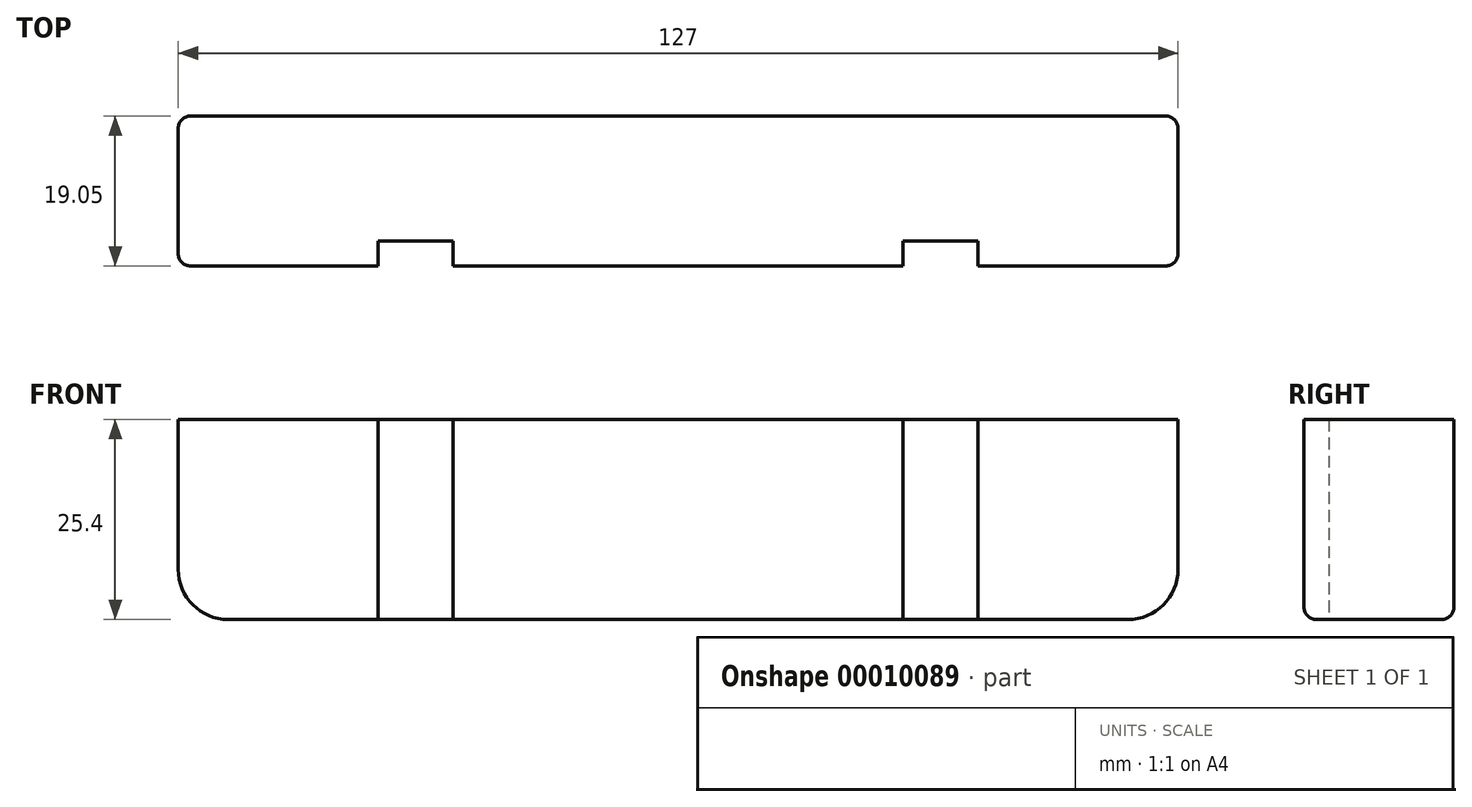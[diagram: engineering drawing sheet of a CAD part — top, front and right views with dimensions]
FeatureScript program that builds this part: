
annotation { "Feature Type Name" : "Feature", "Feature Type Description" : "" }
export const myFeature = defineFeature(function(context is Context, id is Id, definition is map)
    precondition{}
    {
        {
            var Q0;
            Q0=qCreatedBy(makeId("Front.planeOp"),FACE);
            var sketch = newSketch(context, id + "F0", { "sketchPlane" : qUnion([Q0])});
            skLineSegment(sketch, "E0.rect.bottom", {"start": v(63.5, 12.7) * mm, "end": v(-63.5, 12.7) * mm});
            skLineSegment(sketch, "E0.rect.top", {"start": v(63.5, -12.7) * mm, "end": v(-63.5, -12.7) * mm});
            skLineSegment(sketch, "E0.rect.left", {"start": v(63.5, 12.7) * mm, "end": v(63.5, -12.7) * mm});
            skLineSegment(sketch, "E0.rect.right", {"start": v(-63.5, 12.7) * mm, "end": v(-63.5, -12.7) * mm});
            skPoint(sketch, "E0.rect.middle", {"position": v(0, 0) * mm});
            skSolve(sketch);
        }
        {
            var Q0;
            Q0=makeQuery(id+"F0.imprint","IMPRINT",FACE,{"disambiguationData":[TD([[makeQuery(id+"F0.imprint","IMPRINT",EDGE,{"derivedFrom":sQuery(id+"F0.wireOp",EDGE,"E0.rect.bottom")}),1.0]])]});
            extrude(context, id + "F1", {"entities" : qUnion([Q0]), "oppositeDirection" : true, "depth" : 19.05 * mm});
        }
        {
            var Q0;
            Q0=makeQuery(id+"F1.opExtrude","SWEPT_EDGE",EDGE,{"disambiguationData":[OSD([sQuery(id+"F0.wireOp",EDGE,"E0.rect.top"),sQuery(id+"F0.wireOp",EDGE,"E0.rect.left")])]});
            var Q1;
            Q1=makeQuery(id+"F1.opExtrude","SWEPT_EDGE",EDGE,{"disambiguationData":[OSD([sQuery(id+"F0.wireOp",EDGE,"E0.rect.top"),sQuery(id+"F0.wireOp",EDGE,"E0.rect.right")])]});
            fillet(context, id + "F2", {"entities" : qUnion([Q0, Q1]), "radius" : 6.35 * mm, "tangentPropagation" : true, "allowEdgeOverflow" : false});
        }
        {
            var Q0;
            Q0=makeQuery(id+"F1.opExtrude","CAP_EDGE",EDGE,{"disambiguationData":[OSD([sQuery(id+"F0.wireOp",EDGE,"E0.rect.right")])],"isStart":true});
            var Q1;
            {var subQ0=sQuery(id+"F0.wireOp",EDGE,"E0.rect.top");var subQ1=sQuery(id+"F0.wireOp",EDGE,"E0.rect.right");Q1=makeQuery(id+"F2.opFillet","BLEND_EDGE",EDGE,{"blendedFrom":[makeQuery(id+"F1.opExtrude","SWEPT_EDGE",EDGE,{"disambiguationData":[OSD([subQ0,subQ1])]}),makeQuery(id+"F1.opExtrude","CAP_FACE",FACE,{"disambiguationData":[OSD([sQuery(id+"F0.wireOp",EDGE,"E0.rect.bottom"),subQ0,sQuery(id+"F0.wireOp",EDGE,"E0.rect.left"),subQ1])],"isStart":true})],"blendedInto":[makeQuery(id+"F1.opExtrude","CAP_FACE",FACE,{"disambiguationData":[OSD([sQuery(id+"F0.wireOp",EDGE,"E0.rect.bottom"),subQ0,sQuery(id+"F0.wireOp",EDGE,"E0.rect.left"),subQ1])],"isStart":true})]});}
            var Q2;
            Q2=makeQuery(id+"F1.opExtrude","CAP_EDGE",EDGE,{"disambiguationData":[OSD([sQuery(id+"F0.wireOp",EDGE,"E0.rect.top")])],"isStart":true});
            var Q3;
            {var subQ0=sQuery(id+"F0.wireOp",EDGE,"E0.rect.top");var subQ1=sQuery(id+"F0.wireOp",EDGE,"E0.rect.left");Q3=makeQuery(id+"F2.opFillet","BLEND_EDGE",EDGE,{"blendedFrom":[makeQuery(id+"F1.opExtrude","SWEPT_EDGE",EDGE,{"disambiguationData":[OSD([subQ0,subQ1])]}),makeQuery(id+"F1.opExtrude","CAP_FACE",FACE,{"disambiguationData":[OSD([sQuery(id+"F0.wireOp",EDGE,"E0.rect.bottom"),subQ0,subQ1,sQuery(id+"F0.wireOp",EDGE,"E0.rect.right")])],"isStart":true})],"blendedInto":[makeQuery(id+"F1.opExtrude","CAP_FACE",FACE,{"disambiguationData":[OSD([sQuery(id+"F0.wireOp",EDGE,"E0.rect.bottom"),subQ0,subQ1,sQuery(id+"F0.wireOp",EDGE,"E0.rect.right")])],"isStart":true})]});}
            var Q4;
            Q4=makeQuery(id+"F1.opExtrude","CAP_EDGE",EDGE,{"disambiguationData":[OSD([sQuery(id+"F0.wireOp",EDGE,"E0.rect.left")])],"isStart":true});
            var Q5;
            Q5=makeQuery(id+"F1.opExtrude","CAP_EDGE",EDGE,{"disambiguationData":[OSD([sQuery(id+"F0.wireOp",EDGE,"E0.rect.left")])],"isStart":false});
            var Q6;
            {var subQ0=sQuery(id+"F0.wireOp",EDGE,"E0.rect.top");var subQ1=sQuery(id+"F0.wireOp",EDGE,"E0.rect.left");Q6=makeQuery(id+"F2.opFillet","BLEND_EDGE",EDGE,{"blendedFrom":[makeQuery(id+"F1.opExtrude","SWEPT_EDGE",EDGE,{"disambiguationData":[OSD([subQ0,subQ1])]}),makeQuery(id+"F1.opExtrude","CAP_FACE",FACE,{"disambiguationData":[OSD([sQuery(id+"F0.wireOp",EDGE,"E0.rect.bottom"),subQ0,subQ1,sQuery(id+"F0.wireOp",EDGE,"E0.rect.right")])],"isStart":false})],"blendedInto":[makeQuery(id+"F1.opExtrude","CAP_FACE",FACE,{"disambiguationData":[OSD([sQuery(id+"F0.wireOp",EDGE,"E0.rect.bottom"),subQ0,subQ1,sQuery(id+"F0.wireOp",EDGE,"E0.rect.right")])],"isStart":false})]});}
            var Q7;
            Q7=makeQuery(id+"F1.opExtrude","CAP_EDGE",EDGE,{"disambiguationData":[OSD([sQuery(id+"F0.wireOp",EDGE,"E0.rect.top")])],"isStart":false});
            var Q8;
            {var subQ0=sQuery(id+"F0.wireOp",EDGE,"E0.rect.top");var subQ1=sQuery(id+"F0.wireOp",EDGE,"E0.rect.right");Q8=makeQuery(id+"F2.opFillet","BLEND_EDGE",EDGE,{"blendedFrom":[makeQuery(id+"F1.opExtrude","SWEPT_EDGE",EDGE,{"disambiguationData":[OSD([subQ0,subQ1])]}),makeQuery(id+"F1.opExtrude","CAP_FACE",FACE,{"disambiguationData":[OSD([sQuery(id+"F0.wireOp",EDGE,"E0.rect.bottom"),subQ0,sQuery(id+"F0.wireOp",EDGE,"E0.rect.left"),subQ1])],"isStart":false})],"blendedInto":[makeQuery(id+"F1.opExtrude","CAP_FACE",FACE,{"disambiguationData":[OSD([sQuery(id+"F0.wireOp",EDGE,"E0.rect.bottom"),subQ0,sQuery(id+"F0.wireOp",EDGE,"E0.rect.left"),subQ1])],"isStart":false})]});}
            var Q9;
            Q9=makeQuery(id+"F1.opExtrude","CAP_EDGE",EDGE,{"disambiguationData":[OSD([sQuery(id+"F0.wireOp",EDGE,"E0.rect.right")])],"isStart":false});
            fillet(context, id + "F3", {"entities" : qUnion([Q0, Q1, Q2, Q3, Q4, Q5, Q6, Q7, Q8, Q9]), "radius" : 1.59 * mm, "allowEdgeOverflow" : false});
        }
        {
            var Q0;
            Q0=makeQuery(id+"F1.opExtrude","CAP_FACE",FACE,{"disambiguationData":[OSD([sQuery(id+"F0.wireOp",EDGE,"E0.rect.bottom"),sQuery(id+"F0.wireOp",EDGE,"E0.rect.top"),sQuery(id+"F0.wireOp",EDGE,"E0.rect.left"),sQuery(id+"F0.wireOp",EDGE,"E0.rect.right")])],"isStart":true});
            var sketch = newSketch(context, id + "F4", { "sketchPlane" : qUnion([Q0])});
            skLineSegment(sketch, "E1.0", {"start": v(57.15, -12.7) * mm, "end": v(-57.15, -12.7) * mm});
            skLineSegment(sketch, "E2.bottom", {"start": v(-28.57, 12.7) * mm, "end": v(-38.1, 12.7) * mm});
            skLineSegment(sketch, "E2.top", {"start": v(-28.57, -12.7) * mm, "end": v(-38.1, -12.7) * mm});
            skLineSegment(sketch, "E2.left", {"start": v(-28.57, 12.7) * mm, "end": v(-28.57, -12.7) * mm});
            skLineSegment(sketch, "E2.right", {"start": v(-38.1, 12.7) * mm, "end": v(-38.1, -12.7) * mm});
            skLineSegment(sketch, "E3", {"start": v(0, 12.7) * mm, "end": v(0, -12.7) * mm, "construction": true});
            skLineSegment(sketch, "E4.MirrorCS", {"start": v(28.57, 12.7) * mm, "end": v(38.1, 12.7) * mm});
            skLineSegment(sketch, "E5.MirrorCS", {"start": v(28.58, -12.7) * mm, "end": v(38.1, -12.7) * mm});
            skLineSegment(sketch, "E6.MirrorCS", {"start": v(38.1, 12.7) * mm, "end": v(38.1, -12.7) * mm});
            skLineSegment(sketch, "E7.MirrorCS", {"start": v(28.57, 12.7) * mm, "end": v(28.58, -12.7) * mm});
            skSolve(sketch);
        }
        {
            var Q0;
            Q0 = qSketchRegion(id + "F4", true);
            extrude(context, id + "F5", {"entities" : qUnion([Q0]), "operationType" : NewBodyOperationType.REMOVE, "oppositeDirection" : true, "depth" : 3.17 * mm});
        }
    });
